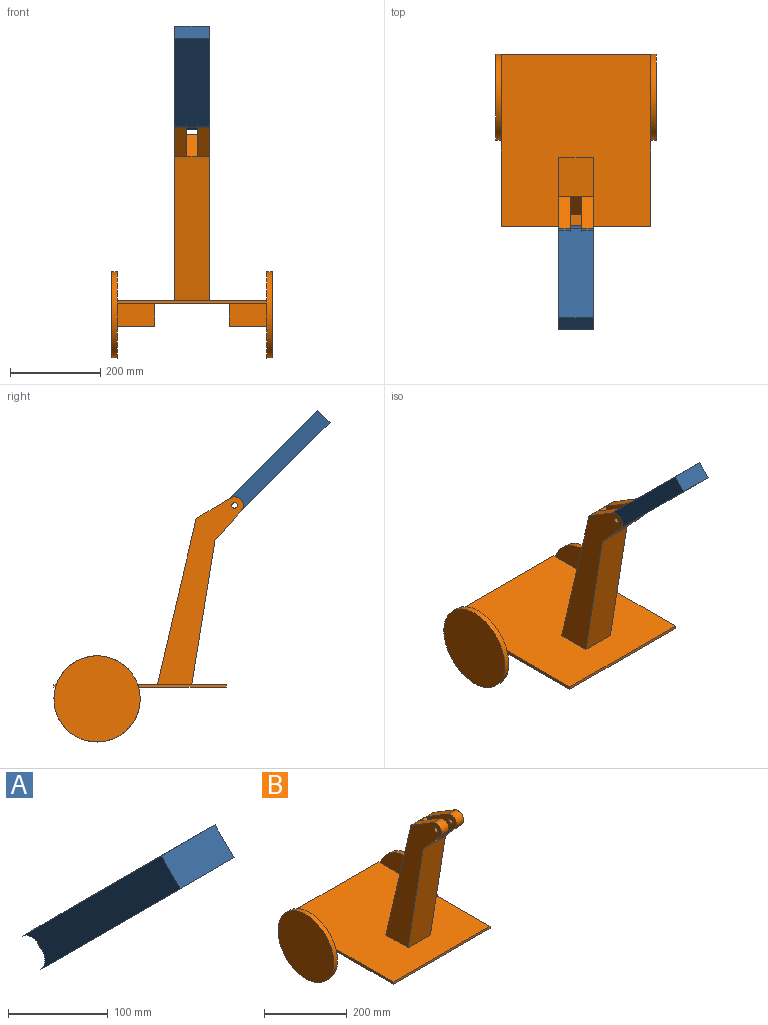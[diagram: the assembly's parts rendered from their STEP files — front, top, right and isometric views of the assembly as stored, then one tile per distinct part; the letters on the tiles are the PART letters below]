
ASSEMBLY  parts=2 mates=1
PART A: 11 faces, bbox 76.2x230.1x230.1 mm
  f0: plane 38.1x38.1mm, normal (1,0,0), area 1013.4mm2, adj f3,f6,f9
  f1: plane 38.1x38.1mm, normal (-1,0,0), area 1013.4mm2, adj f3,f6,f8
  f2: plane 197.57x197.57mm, normal (0,-0.71,-0.71), area 21290.3mm2, adj f3,f5,f7,f8,f9,f10
  f3: cylinder r=19.05mm len=32.52mm, axis (-1,0,0), area 1520.1mm2, adj f0,f1,f2,f4
  f4: plane 197.57x197.57mm, normal (0,0.71,0.71), area 21290.3mm2, adj f3,f5,f7,f8,f9,f10
  f5: plane 76.2x26.94mm, normal (0,-0.71,0.71), area 2903.2mm2, adj f2,f4,f7,f10
  f6: cylinder r=6.35mm len=25.4mm, axis (1,0,0), area 1013.4mm2, adj f0,f1
  f7: plane 224.51x224.51mm, normal (-1,0,0), area 10075.1mm2, adj f2,f4,f5,f8
  f8: cylinder r=19.05mm len=32.52mm, axis (-1,0,0), area 1520.1mm2, adj f1,f2,f4,f7
  f9: cylinder r=19.05mm len=32.52mm, axis (-1,0,0), area 1520.1mm2, adj f0,f2,f4,f10
  f10: plane 224.51x224.51mm, normal (1,0,0), area 10075.1mm2, adj f2,f4,f5,f9
PART B: 41 faces, bbox 355.6x418.3x542 mm
  f0: plane 76.2x48.94mm, normal (0,-0.77,0.63), area 1609mm2, adj f25,f26,f27,f28,f33,f37,f39,f40
  f1: plane 6.35x5.45mm, normal (1,0,0), area 28mm2, adj f4,f7,f8,f22
  f2: plane 195.95x6.35mm, normal (-1,0,0), area 1237.7mm2, adj f6,f7,f8,f18
  f3: plane 195.95x6.35mm, normal (1,0,0), area 1237.7mm2, adj f6,f7,f8,f22
  f4: plane 330.2x6.35mm, normal (0,1,0), area 2096.8mm2, adj f1,f5,f7,f8
  f5: plane 6.35x5.45mm, normal (-1,0,0), area 28mm2, adj f4,f7,f8,f18
  f6: plane 330.2x6.35mm, normal (0,-1,0), area 2096.8mm2, adj f2,f3,f7,f8
  f7: plane 381x330.2mm, normal (0,0,1), area 120027.6mm2, adj f1,f2,f3,f4,f5,f6,f20,f21
  f8: plane 381x330.2mm, normal (0,0,-1), area 117419.1mm2, adj f1,f2,f3,f4,f5,f6,f9,f10
  f9: plane 82.55x50.8mm, normal (0,1,0), area 4193.5mm2, adj f8,f10,f12,f17
  f10: plane 50.8x50.8mm, normal (1,0,0), area 2580.6mm2, adj f8,f9,f11,f12
  f11: plane 82.55x50.8mm, normal (0,-1,0), area 4193.5mm2, adj f8,f10,f12,f17
  f12: plane 82.55x50.8mm, normal (0,0,-1), area 4193.5mm2, adj f9,f10,f11,f17
  f13: plane 82.55x50.8mm, normal (0,-1,0), area 4193.5mm2, adj f8,f14,f16,f24
  f14: plane 50.8x50.8mm, normal (-1,0,0), area 2580.6mm2, adj f8,f13,f15,f16
  f15: plane 82.55x50.8mm, normal (0,1,0), area 4193.5mm2, adj f8,f14,f16,f24
  f16: plane 82.55x50.8mm, normal (0,0,-1), area 4193.5mm2, adj f13,f14,f15,f24
  f17: plane 190.5x120.65mm, normal (1,0,0), area 16451.2mm2, adj f8,f9,f11,f12,f18
  f18: cylinder r=95.25mm len=190.5mm, axis (1,0,0), area 7600.6mm2, adj f2,f5,f17,f19,f20
  f19: plane 190.5x190.5mm, normal (-1,0,0), area 28502.3mm2, adj f18
  f20: plane 179.61x63.5mm, normal (1,0,0), area 8316.7mm2, adj f7,f18
  f21: plane 179.61x63.5mm, normal (-1,0,0), area 8316.7mm2, adj f7,f22
  f22: cylinder r=95.25mm len=190.5mm, axis (-1,0,0), area 7600.6mm2, adj f1,f3,f21,f23,f24
  f23: plane 190.5x190.5mm, normal (1,0,0), area 28502.3mm2, adj f22
  f24: plane 190.5x120.65mm, normal (-1,0,0), area 16451.2mm2, adj f8,f13,f15,f16,f22
  f25: plane 415.03x189.55mm, normal (1,0,0), area 26473.3mm2, adj f0,f7,f29,f32,f33,f34,f35,f38
  f26: plane 415.03x189.55mm, normal (-1,0,0), area 26473.3mm2, adj f0,f7,f30,f31,f33,f34,f36,f38
  f27: plane 103.04x96.45mm, normal (-1,0,0), area 4653.9mm2, adj f0,f29,f32,f35,f37,f38,f39
  f28: plane 103.04x96.45mm, normal (1,0,0), area 4653.9mm2, adj f0,f30,f31,f36,f37,f38,f40
  f29: cylinder r=19.05mm len=31.18mm, axis (1,0,0), area 1329.1mm2, adj f25,f27,f35,f39
  f30: cylinder r=19.05mm len=31.18mm, axis (-1,0,0), area 1329.1mm2, adj f26,f28,f36,f40
  f31: cylinder r=6.35mm len=25.4mm, axis (1,0,0), area 1013.4mm2, adj f26,f28
  f32: cylinder r=6.35mm len=25.4mm, axis (1,0,0), area 1013.4mm2, adj f25,f27
  f33: plane 318.56x76.2mm, normal (0,-0.99,-0.16), area 24587.8mm2, adj f0,f7,f25,f26
  f34: plane 366.4x85.55mm, normal (0,0.97,0.23), area 28671mm2, adj f7,f25,f26,f38
  f35: plane 74.9x45.26mm, normal (0,0.52,0.86), area 2222.8mm2, adj f25,f27,f29,f38
  f36: plane 74.9x45.26mm, normal (0,0.52,0.86), area 2222.8mm2, adj f26,f28,f30,f38
  f37: plane 25.4x0.59mm, normal (0,0.23,0.97), area 15.5mm2, adj f0,f27,f28,f38
  f38: plane 76.2x1.16mm, normal (0,0.71,0.71), area 117.5mm2, adj f25,f26,f27,f28,f34,f35,f36,f37
  f39: plane 65.26x57.98mm, normal (0,-0.75,-0.66), area 2217.3mm2, adj f0,f25,f27,f29
  f40: plane 65.26x57.98mm, normal (0,-0.75,-0.66), area 2217.3mm2, adj f0,f26,f28,f30
PLACE A t=(-212.54,40.96,-69.02)mm
PLACE B t=(-212.54,263.2,-457.87)mm
MATE revolute A.f3 <-> B.f29  axis (1,0,0) through (-225.24,54.43,-55.55)mm
